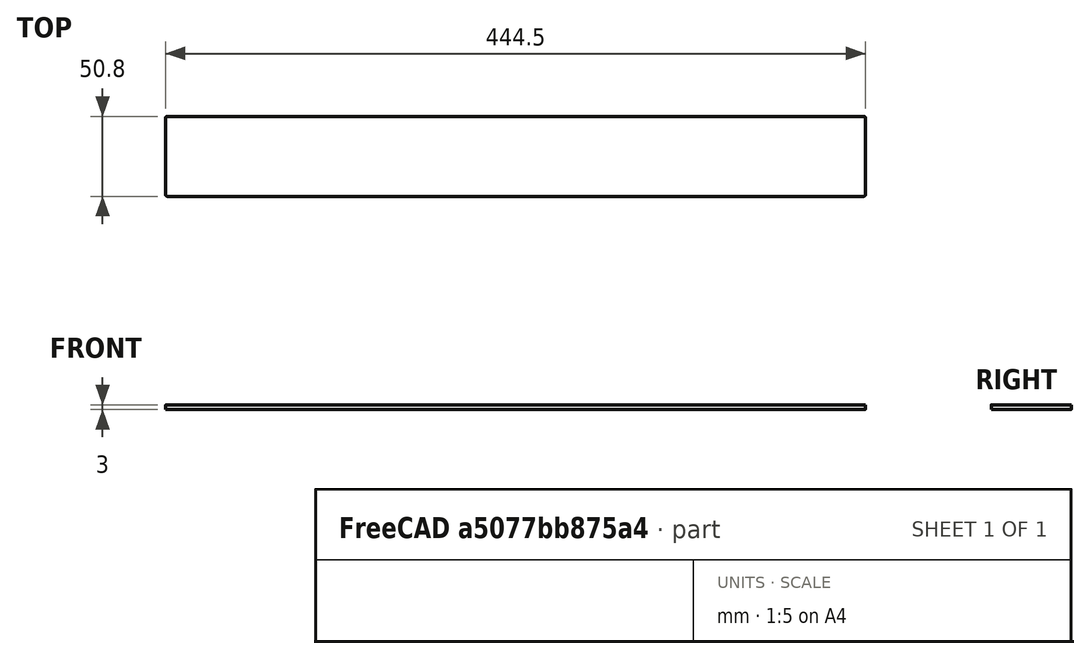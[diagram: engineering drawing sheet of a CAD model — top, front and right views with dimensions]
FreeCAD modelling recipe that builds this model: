
FCSTD DOCUMENT  (FreeCAD 0.20R29603 (Git))
Label: 17p5in_x_2in
License: All rights reserved
LicenseURL: http://en.wikipedia.org/wiki/All_rights_reserved
objects: Spreadsheet::Sheet×1, Sketcher::SketchObject×1, PartDesign::Pad×1, PartDesign::Body×1
note: 4 computed .brp shape members not serialized (recipe doc carries the construction recipe); baked Part::Feature solids carry a one-line shape summary decoded from their .brp

FEATURE [Spreadsheet::Sheet] Spreadsheet
  cells = A2=Length; B2(Length)==17.5in; A3=Width; B3(Width)==2in; A4=Thickness; B4(Thickness)==3mm; A5=FilletRadius; B5(FilletRadius)==1mm
FEATURE [Sketcher::SketchObject] Sketch
  FullyConstrained = true
  MapMode = 5
  Support = -> [XY_Plane]
  expr: Constraints[19] = Spreadsheet.FilletRadius
  expr: Constraints[21] = Spreadsheet.Length
  expr: Constraints[22] = Spreadsheet.Width
  sketch-geometry (10):
    g0: ArcOfCircle CenterX=-221.25 CenterY=24.4 CenterZ=0 NormalX=0 NormalY=0 NormalZ=1 AngleXU=0 Radius=1 StartAngle=1.5708 EndAngle=3.14159
    g1: LineSegment StartX=-221.25 StartY=25.4 StartZ=0 EndX=221.25 EndY=25.4 EndZ=0
    g2: ArcOfCircle CenterX=221.25 CenterY=24.4 CenterZ=0 NormalX=0 NormalY=0 NormalZ=1 AngleXU=0 Radius=1 StartAngle=0 EndAngle=1.5708
    g3: LineSegment StartX=222.25 StartY=24.4 StartZ=0 EndX=222.25 EndY=-24.4 EndZ=0
    g4: ArcOfCircle CenterX=221.25 CenterY=-24.4 CenterZ=0 NormalX=0 NormalY=0 NormalZ=1 AngleXU=0 Radius=1 StartAngle=4.71239 EndAngle=6.28319
    g5: LineSegment StartX=221.25 StartY=-25.4 StartZ=0 EndX=-221.25 EndY=-25.4 EndZ=0
    g6: ArcOfCircle CenterX=-221.25 CenterY=-24.4 CenterZ=0 NormalX=0 NormalY=0 NormalZ=1 AngleXU=0 Radius=1 StartAngle=3.14159 EndAngle=4.71239
    g7: LineSegment StartX=-222.25 StartY=-24.4 StartZ=0 EndX=-222.25 EndY=24.4 EndZ=0
    g8: GeomPoint X=-222.25 Y=25.4 Z=0
    g9: GeomPoint X=222.25 Y=-25.4 Z=0
  constraints (23):
    c: Tangent(g0,g1) = 1.5708
    c: Tangent(g1,g2) = 1.5708
    c: Tangent(g2,g3) = 1.5708
    c: Tangent(g3,g4) = 1.5708
    c: Tangent(g4,g5) = 1.5708
    c: Tangent(g5,g6) = 1.5708
    c: Tangent(g6,g7) = 1.5708
    c: Tangent(g7,g0) = 1.5708
    c: Horizontal(g1)
    c: Horizontal(g5)
    c: Vertical(g3)
    c: Vertical(g7)
    c: Equal(g0,g2)
    c: Equal(g2,g4)
    c: Equal(g4,g6)
    c: PointOnObject(g8,g1)
    c: PointOnObject(g8,g7)
    c: PointOnObject(g9,g3)
    c: PointOnObject(g9,g5)
    c: Radius(g4) = 1
    c: Symmetric(g8,g9,g-1)
    c: DistanceX(g6,g3) = 444.5
    c: DistanceY(g4,g1) = 50.8
FEATURE [PartDesign::Pad] Pad
  Direction = (0,0,1)
  Length = 3
  Length2 = 10
  Profile = -> Sketch
  ReferenceAxis = -> Sketch [N_Axis]
  Type = 0
  expr: Length = Spreadsheet.Thickness
FEATURE [PartDesign::Body] Body
  Group = -> [Sketch,Pad]
  Origin = -> Origin
  Tip = -> Pad
